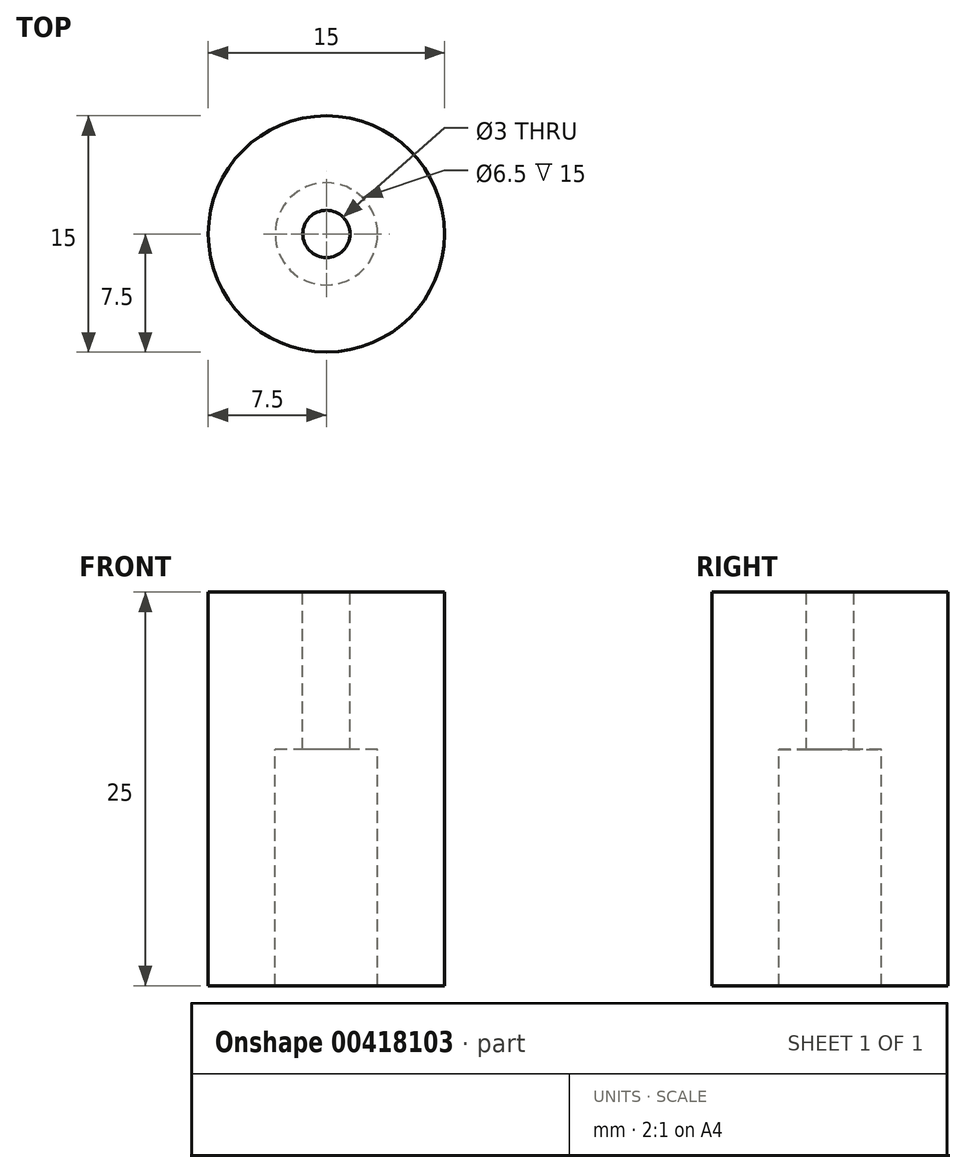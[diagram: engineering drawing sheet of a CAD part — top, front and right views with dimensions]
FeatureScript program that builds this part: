
annotation { "Feature Type Name" : "Feature", "Feature Type Description" : "" }
export const myFeature = defineFeature(function(context is Context, id is Id, definition is map)
    precondition{}
    {
        {
            var Q0;
            Q0=qCreatedBy(makeId("Top.planeOp"),FACE);
            var sketch = newSketch(context, id + "F0", { "sketchPlane" : qUnion([Q0])});
            skCircle(sketch, "E0", {"center": v(0, 0) * mm, "radius": 3 * mm});
            skCircle(sketch, "E1", {"center": v(0, 0) * mm, "radius": 7.5 * mm});
            skSolve(sketch);
        }
        {
            var Q0;
            Q0 = qSketchRegion(id + "F0", true);
            var Q1;
            Q1=makeQuery(id+"F0.imprint","IMPRINT",FACE,{"disambiguationData":[TD([[makeQuery(id+"F0.imprint","IMPRINT",EDGE,{"derivedFrom":sQuery(id+"F0.wireOp",EDGE,"E0")}),-1.0]])]});
            var Q2;
            Q2=makeQuery(id+"F0.imprint","IMPRINT",FACE,{"disambiguationData":[TD([[makeQuery(id+"F0.imprint","IMPRINT",EDGE,{"derivedFrom":sQuery(id+"F0.wireOp",EDGE,"E0")}),1.0]])]});
            extrude(context, id + "F1", {"entities" : qUnion([Q0, Q1, Q2]), "depth" : 25 * mm});
        }
        {
            var Q0;
            Q0=sQuery(id+"F0.wireOp",VERTEX,"E0.center");
            var Q1;
            Q1=makeQuery(id+"F1.opExtrude","SWEPT_BODY",BODY,{"disambiguationData":[OSD([sQuery(id+"F0.wireOp",EDGE,"E1")])]});
            hole(context, id + "F2", {"style" : HoleStyle.C_BORE, "endStyle" : HoleEndStyle.THROUGH, "oppositeDirection" : true, "holeDiameter" : 3 * mm, "cBoreDiameter" : 6.5 * mm, "cBoreDepth" : 15 * mm, "isTappedThrough" : true, "tappedDepth" : 12 * mm, "tapClearance" : 3, "locations" : qUnion([Q0]), "scope" : qUnion([Q1]), "startStyle" : HoleStartStyle.PART});
        }
    });
